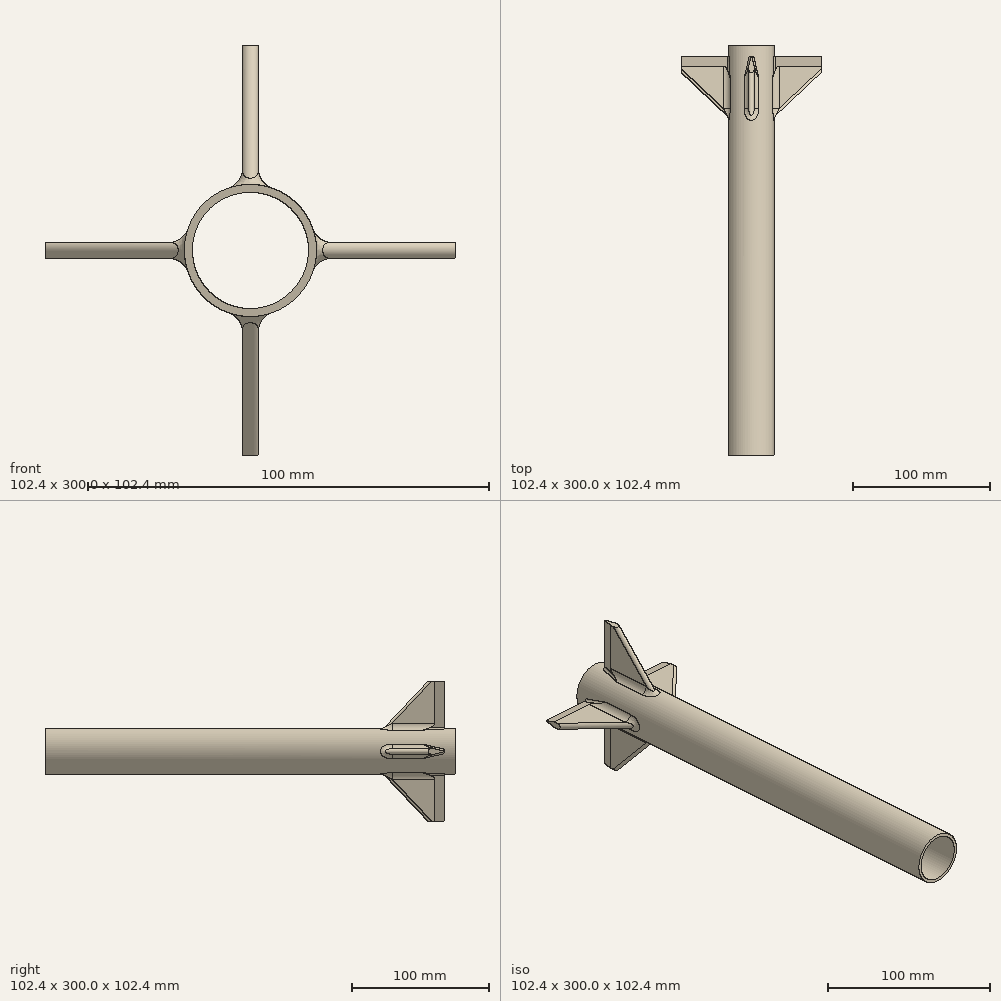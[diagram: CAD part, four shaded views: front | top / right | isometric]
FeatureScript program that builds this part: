
annotation { "Feature Type Name" : "Feature", "Feature Type Description" : "" }
export const myFeature = defineFeature(function(context is Context, id is Id, definition is map)
    precondition{}
    {
        {
            var Q0;
            Q0=qCreatedBy(makeId("Front.planeOp"),FACE);
            var sketch = newSketch(context, id + "F0", { "sketchPlane" : qUnion([Q0])});
            skCircle(sketch, "E0", {"center": v(0, 0) * mm, "radius": 16.5 * mm});
            skCircle(sketch, "E1", {"center": v(0, 0) * mm, "radius": 14.5 * mm});
            skPoint(sketch, "E2", {"position": v(16.5, 0) * mm});
            skSolve(sketch);
        }
        {
            var Q0;
            Q0 = qSketchRegion(id + "F0", true);
            extrude(context, id + "F1", {"entities" : qUnion([Q0]), "endBound" : BoundingType.SYMMETRIC, "depth" : 300 * mm, "offsetDistance" : 25 * mm});
        }
        {
            var Q0;
            Q0=qCreatedBy(makeId("Right.planeOp"),FACE);
            var sketch = newSketch(context, id + "F2", { "sketchPlane" : qUnion([Q0])});
            skLineSegment(sketch, "E3", {"start": v(97, 16.2) * mm, "end": v(130, 51.2) * mm});
            skLineSegment(sketch, "E4", {"start": v(130, 51.2) * mm, "end": v(142, 51.2) * mm});
            skLineSegment(sketch, "E5", {"start": v(142, 51.2) * mm, "end": v(142, 16.2) * mm});
            skLineSegment(sketch, "E6", {"start": v(142, 16.2) * mm, "end": v(97, 16.2) * mm});
            skSolve(sketch);
        }
        {
            var Q0;
            Q0=makeQuery(id+"F2.imprint","IMPRINT",FACE,{"disambiguationData":[TD([[makeQuery(id+"F2.imprint","IMPRINT",EDGE,{"derivedFrom":sQuery(id+"F2.wireOp",EDGE,"E3")}),-1.0]])]});
            extrude(context, id + "F3", {"entities" : qUnion([Q0]), "endBound" : BoundingType.SYMMETRIC, "depth" : 4 * mm, "offsetDistance" : 25 * mm});
        }
        {
            var Q0;
            Q0=makeQuery(id+"F3.opExtrude","CAP_EDGE",EDGE,{"disambiguationData":[OSD([sQuery(id+"F2.wireOp",EDGE,"E3")])],"isStart":false});
            fillet(context, id + "F4", {"entities" : qUnion([Q0]), "radius" : 2 * mm, "tangentPropagation" : true, "allowEdgeOverflow" : false});
        }
        {
            var Q0;
            Q0=makeQuery(id+"F3.opExtrude","CAP_EDGE",EDGE,{"disambiguationData":[OSD([sQuery(id+"F2.wireOp",EDGE,"E3")])],"isStart":true});
            fillet(context, id + "F5", {"entities" : qUnion([Q0]), "radius" : 2 * mm, "tangentPropagation" : true, "allowEdgeOverflow" : false});
        }
        {
            var Q0;
            Q0=makeQuery(id+"F3.opExtrude","CAP_EDGE",EDGE,{"disambiguationData":[OSD([sQuery(id+"F2.wireOp",EDGE,"E5")])],"isStart":false});
            chamfer(context, id + "F6", {"entities" : qUnion([Q0]), "chamferType" : ChamferType.TWO_OFFSETS, "width1" : 1.8 * mm, "oppositeDirection" : false, "width2" : 7 * mm, "tangentPropagation" : true});
        }
        {
            var Q0;
            Q0=makeQuery(id+"F3.opExtrude","CAP_EDGE",EDGE,{"disambiguationData":[OSD([sQuery(id+"F2.wireOp",EDGE,"E5")])],"isStart":true});
            chamfer(context, id + "F7", {"entities" : qUnion([Q0]), "chamferType" : ChamferType.TWO_OFFSETS, "width1" : 1.8 * mm, "oppositeDirection" : true, "width2" : 7 * mm, "tangentPropagation" : true});
        }
        {
            var Q0;
            Q0=makeQuery(id+"F3.opExtrude","SWEPT_BODY",BODY,{"disambiguationData":[OSD([sQuery(id+"F2.wireOp",EDGE,"E3"),sQuery(id+"F2.wireOp",EDGE,"E4"),sQuery(id+"F2.wireOp",EDGE,"E5"),sQuery(id+"F2.wireOp",EDGE,"E6")])]});
            var Q1;
            Q1=makeQuery(id+"F1.opExtrude","SWEPT_BODY",BODY,{"disambiguationData":[OSD([sQuery(id+"F0.wireOp",EDGE,"E0"),sQuery(id+"F0.wireOp",EDGE,"E1")])]});
            booleanBodies(context, id + "F8", {"operationType" : BooleanOperationType.UNION, "tools" : qUnion([Q0, Q1])});
        }
        {
            var Q0;
            Q0=makeQuery(id+"F8.opBoolean","INTERSECT",EDGE,{"derivedFrom":[makeQuery(id+"F1.opExtrude","SWEPT_FACE",FACE,{"disambiguationData":[OSD([sQuery(id+"F0.wireOp",EDGE,"E0")])]}),makeQuery(id+"F3.opExtrude","CAP_FACE",FACE,{"disambiguationData":[OSD([sQuery(id+"F2.wireOp",EDGE,"E3"),sQuery(id+"F2.wireOp",EDGE,"E4"),sQuery(id+"F2.wireOp",EDGE,"E5"),sQuery(id+"F2.wireOp",EDGE,"E6")])],"isStart":false})]});
            fillet(context, id + "F9", {"entities" : qUnion([Q0]), "radius" : 5 * mm, "tangentPropagation" : true, "allowEdgeOverflow" : false});
        }
        {
            var Q0;
            Q0=makeQuery(id+"F8.opBoolean","INTERSECT",EDGE,{"derivedFrom":[makeQuery(id+"F1.opExtrude","SWEPT_FACE",FACE,{"disambiguationData":[OSD([sQuery(id+"F0.wireOp",EDGE,"E0")])]}),makeQuery(id+"F6.opChamfer","BLEND_FACE",FACE,{"disambiguationData":[OSD([sQuery(id+"F2.wireOp",EDGE,"E5")])]})]});
            fillet(context, id + "F10", {"entities" : qUnion([Q0]), "radius" : 1.5 * mm, "tangentPropagation" : true, "allowEdgeOverflow" : false});
        }
        {
            var Q0;
            Q0=makeQuery(id+"F8.opBoolean","INTERSECT",EDGE,{"derivedFrom":[makeQuery(id+"F1.opExtrude","SWEPT_FACE",FACE,{"disambiguationData":[OSD([sQuery(id+"F0.wireOp",EDGE,"E0")])]}),makeQuery(id+"F7.opChamfer","BLEND_FACE",FACE,{"disambiguationData":[OSD([sQuery(id+"F2.wireOp",EDGE,"E5")])]})]});
            fillet(context, id + "F11", {"entities" : qUnion([Q0]), "radius" : 1.5 * mm, "tangentPropagation" : true, "allowEdgeOverflow" : false});
        }
        {
            var Q0;
            Q0=makeQuery(id+"F3.opExtrude","SWEPT_BODY",BODY,{"disambiguationData":[OSD([sQuery(id+"F2.wireOp",EDGE,"E3"),sQuery(id+"F2.wireOp",EDGE,"E4"),sQuery(id+"F2.wireOp",EDGE,"E5"),sQuery(id+"F2.wireOp",EDGE,"E6")])]});
            var Q1;
            Q1=makeQuery(id+"F1.opExtrude","SWEPT_FACE",FACE,{"disambiguationData":[OSD([sQuery(id+"F0.wireOp",EDGE,"E0")])]});
            circularPattern(context, id + "F12", {"operationType" : NewBodyOperationType.ADD, "entities" : qUnion([Q0]), "axis" : qUnion([Q1]), "angle" : 360 * degree, "instanceCount" : 4, "equalSpace" : true});
        }
    });
